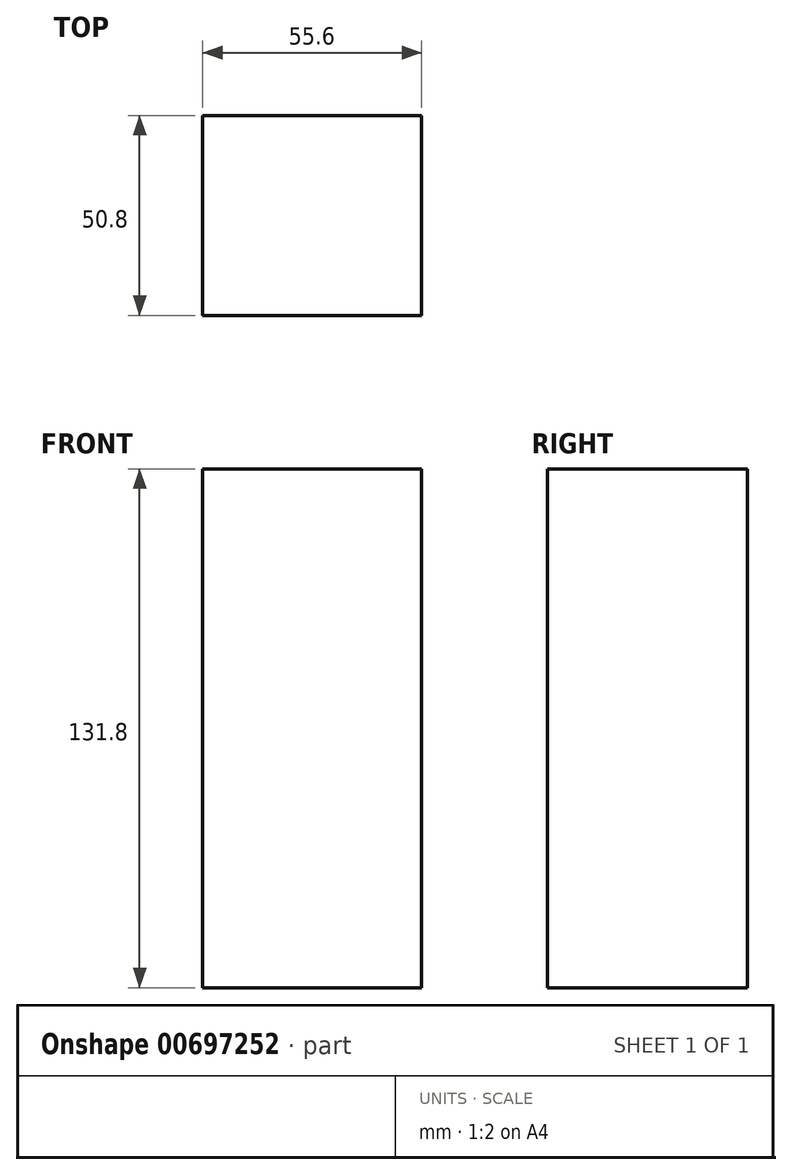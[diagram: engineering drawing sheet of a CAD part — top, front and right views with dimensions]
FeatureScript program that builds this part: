
annotation { "Feature Type Name" : "Feature", "Feature Type Description" : "" }
export const myFeature = defineFeature(function(context is Context, id is Id, definition is map)
    precondition{}
    {
        {
            var Q0;
            Q0=qCreatedBy(makeId("Front.planeOp"),FACE);
            var sketch = newSketch(context, id + "F0", { "sketchPlane" : qUnion([Q0])});
            skLineSegment(sketch, "E0.bottom", {"start": v(18.64, 11.33) * mm, "end": v(-36.96, 11.33) * mm});
            skLineSegment(sketch, "E0.top", {"start": v(18.64, -24.9) * mm, "end": v(-36.96, -24.9) * mm});
            skLineSegment(sketch, "E0.left", {"start": v(18.64, 11.33) * mm, "end": v(18.64, -24.9) * mm});
            skLineSegment(sketch, "E0.right", {"start": v(-36.96, 11.33) * mm, "end": v(-36.96, -24.9) * mm});
            skSolve(sketch);
        }
        {
            var Q0;
            Q0 = qSketchRegion(id + "F0", true);
            extrude(context, id + "F1", {"entities" : qUnion([Q0]), "depth" : 25.4 * mm, "offsetDistance" : 25.4 * mm});
        }
        {
            var Q0;
            Q0=makeQuery(id+"F1.opExtrude","CAP_FACE",FACE,{"disambiguationData":[OSD([sQuery(id+"F0.wireOp",EDGE,"E0.bottom"),sQuery(id+"F0.wireOp",EDGE,"E0.top"),sQuery(id+"F0.wireOp",EDGE,"E0.left"),sQuery(id+"F0.wireOp",EDGE,"E0.right")])],"isStart":false});
            extrude(context, id + "F2", {"entities" : qUnion([Q0]), "operationType" : NewBodyOperationType.ADD, "depth" : 25.4 * mm, "offsetDistance" : 25.4 * mm});
        }
        {
            var Q0;
            {var subQ0=sQuery(id+"F0.wireOp",EDGE,"E0.bottom");Q0=makeQuery(id+"F2.boolean.opBoolean","MERGE",FACE,{"derivedFrom":[makeQuery(id+"F1.opExtrude","SWEPT_FACE",FACE,{"disambiguationData":[OSD([subQ0])]}),makeQuery(id+"F2.opExtrude","SWEPT_FACE",FACE,{"disambiguationData":[OSD([subQ0])]})]});}
            extrude(context, id + "F3", {"entities" : qUnion([Q0]), "operationType" : NewBodyOperationType.ADD, "depth" : 95.57 * mm, "offsetDistance" : 25.4 * mm});
        }
    });
